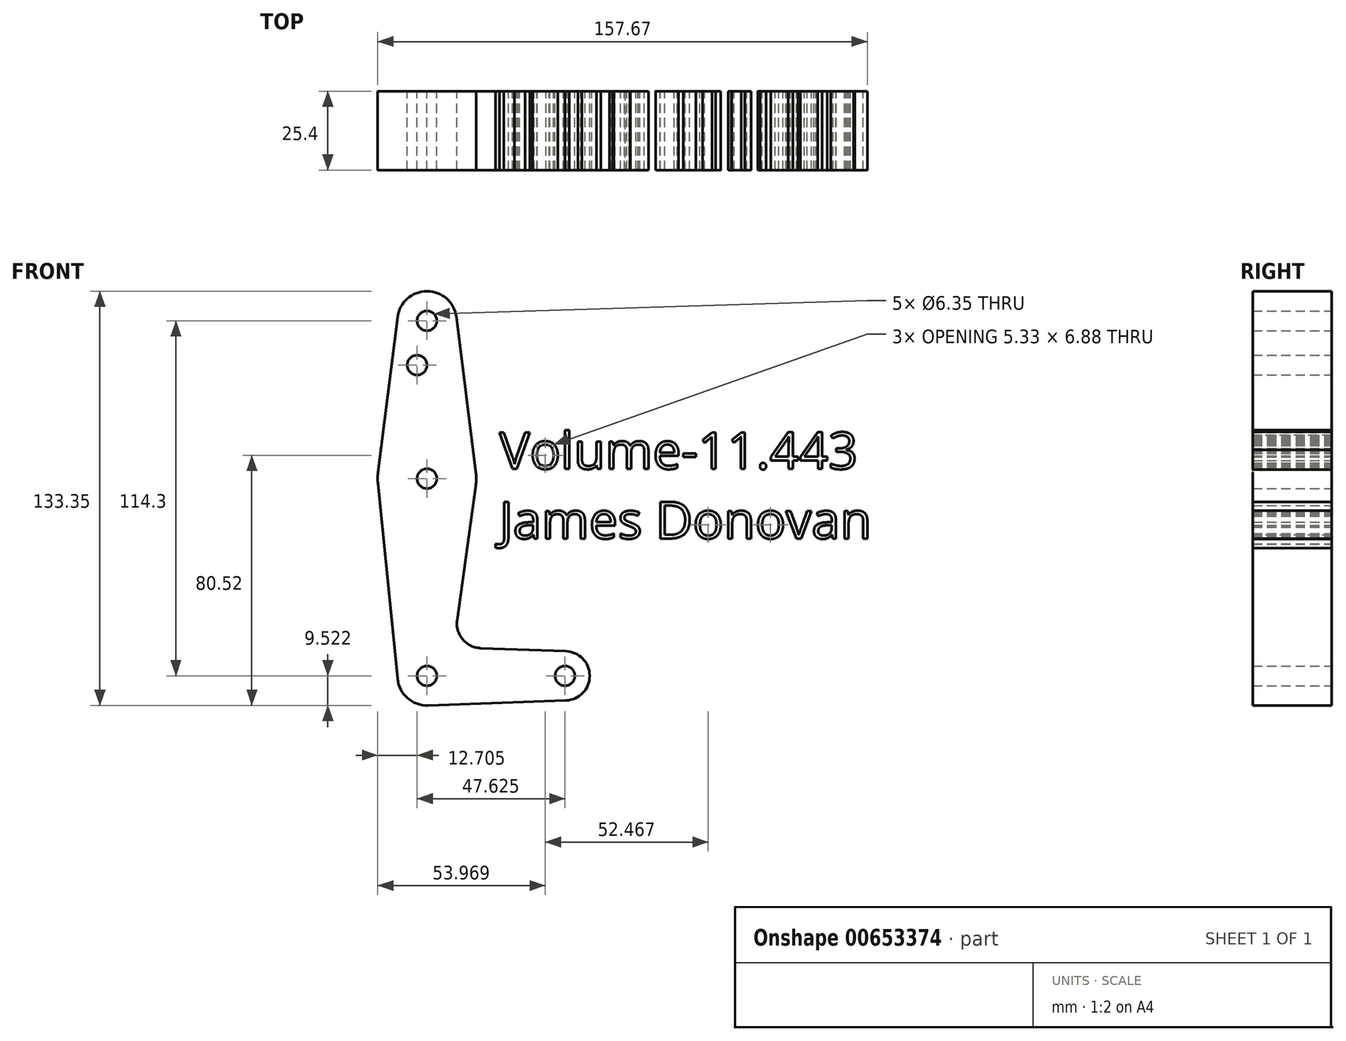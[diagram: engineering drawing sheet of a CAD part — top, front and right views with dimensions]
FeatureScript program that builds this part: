
annotation { "Feature Type Name" : "Feature", "Feature Type Description" : "" }
export const myFeature = defineFeature(function(context is Context, id is Id, definition is map)
    precondition{}
    {
        {
            var Q0;
            Q0=qCreatedBy(makeId("Front.planeOp"),FACE);
            var sketch = newSketch(context, id + "F0", { "sketchPlane" : qUnion([Q0])});
            skLineSegment(sketch, "E0", {"start": v(-44.45, 99.55) * mm, "end": v(-44.45, 48.75) * mm});
            skLineSegment(sketch, "E1", {"start": v(-44.45, 48.75) * mm, "end": v(-44.45, -14.75) * mm});
            skLineSegment(sketch, "E2", {"start": v(-44.45, -14.75) * mm, "end": v(0, -14.75) * mm});
            skCircle(sketch, "E3", {"center": v(-44.45, 99.55) * mm, "radius": 9.53 * mm});
            skCircle(sketch, "E4", {"center": v(-44.45, 48.75) * mm, "radius": 15.88 * mm});
            skCircle(sketch, "E5", {"center": v(-44.45, -14.75) * mm, "radius": 9.53 * mm});
            skCircle(sketch, "E6", {"center": v(0, -14.75) * mm, "radius": 7.94 * mm});
            skLineSegment(sketch, "E7", {"start": v(-35, 100.74) * mm, "end": v(-28.7, 50.74) * mm});
            skLineSegment(sketch, "E8", {"start": v(-53.9, 100.74) * mm, "end": v(-60.2, 50.74) * mm});
            skLineSegment(sketch, "E9", {"start": v(-60.25, 47.16) * mm, "end": v(-53.93, -15.7) * mm});
            skLineSegment(sketch, "E10", {"start": v(-28.71, 46.67) * mm, "end": v(-34.75, 3.2) * mm});
            skLineSegment(sketch, "E11", {"start": v(-27.16, -5.83) * mm, "end": v(0.28, -6.82) * mm});
            skLineSegment(sketch, "E12", {"start": v(-44.1, -24.27) * mm, "end": v(0.28, -22.68) * mm});
            skArc(sketch, "E13.filletArc", {"start": v(-34.75, 3.2) * mm, "mid": v(-32.97, -3) * mm, "end": v(-27.16, -5.83) * mm});
            skCircle(sketch, "E14", {"center": v(-44.45, 99.55) * mm, "radius": 3.18 * mm});
            skCircle(sketch, "E15", {"center": v(-47.63, 85.28) * mm, "radius": 3.18 * mm});
            skCircle(sketch, "E16", {"center": v(-44.45, 48.75) * mm, "radius": 3.18 * mm});
            skCircle(sketch, "E17", {"center": v(-44.45, -14.75) * mm, "radius": 3.18 * mm});
            skCircle(sketch, "E18", {"center": v(0, -14.75) * mm, "radius": 3.18 * mm});
            skSolve(sketch);
        }
        {
            var Q0;
            Q0=qCreatedBy(makeId("Front.planeOp"),FACE);
            var sketch = newSketch(context, id + "F1", { "sketchPlane" : qUnion([Q0])});
            skText(sketch, "E19", { "text": "Volume-11.443\nJames Donovan\n", "fontName": "OpenSans-Regular.ttf"});
            const initialGuessF1  = {"E19": [-0.02114, 0.05185, 1, 0, 0.01186]};
            skSetInitialGuess(sketch, initialGuessF1);
            skSolve(sketch);
        }
        {
            var Q0;
            Q0 = qSketchRegion(id + "F1", true);
            var Q1;
            Q1 = qSketchRegion(id + "F0", true);
            var Q2;
            {var subQ0=sQuery(id+"F0.wireOp",EDGE,"E5");var subQ1=sQuery(id+"F0.wireOp",EDGE,"E1");var subQ2=makeQuery(id+"F0.imprint","INTERSECT",VERTEX,{"derivedFrom":[subQ1,subQ0]});Q2=makeQuery(id+"F0.imprint","IMPRINT",FACE,{"disambiguationData":[TD([[makeQuery(id+"F0.imprint","IMPRINT",EDGE,{"disambiguationData":[TD([[subQ2,-1.0]])],"derivedFrom":subQ1}),1.0]])]});}
            extrude(context, id + "F2", {"entities" : qUnion([Q0, Q1, Q2]), "depth" : 25.4 * mm, "offsetDistance" : 25.4 * mm});
        }
    });
